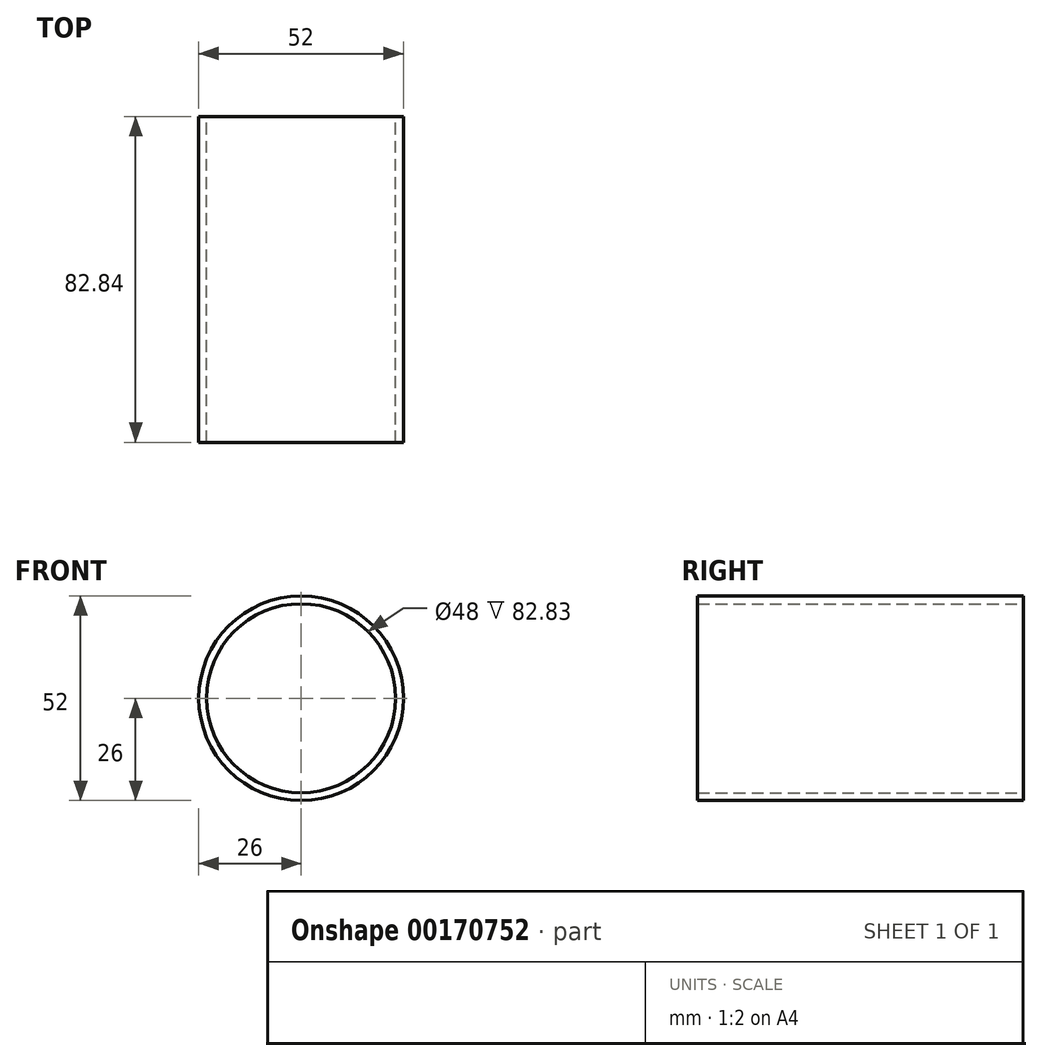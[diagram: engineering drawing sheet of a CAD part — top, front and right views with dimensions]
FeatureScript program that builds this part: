
annotation { "Feature Type Name" : "Feature", "Feature Type Description" : "" }
export const myFeature = defineFeature(function(context is Context, id is Id, definition is map)
    precondition{}
    {
        {
            var Q0;
            Q0=qCreatedBy(makeId("Front.planeOp"),FACE);
            var sketch = newSketch(context, id + "F0", { "sketchPlane" : qUnion([Q0])});
            skCircle(sketch, "E0", {"center": v(0, 0) * mm, "radius": 26 * mm});
            skCircle(sketch, "E1", {"center": v(0, 0) * mm, "radius": 24 * mm});
            skSolve(sketch);
        }
        {
            var Q0;
            Q0=qSketchRegion(id+"F0",true);
            extrude(context, id + "F1", {"entities" : qUnion([Q0]), "depth" : 82.83 * mm, "symmetric" : true});
        }
    });
